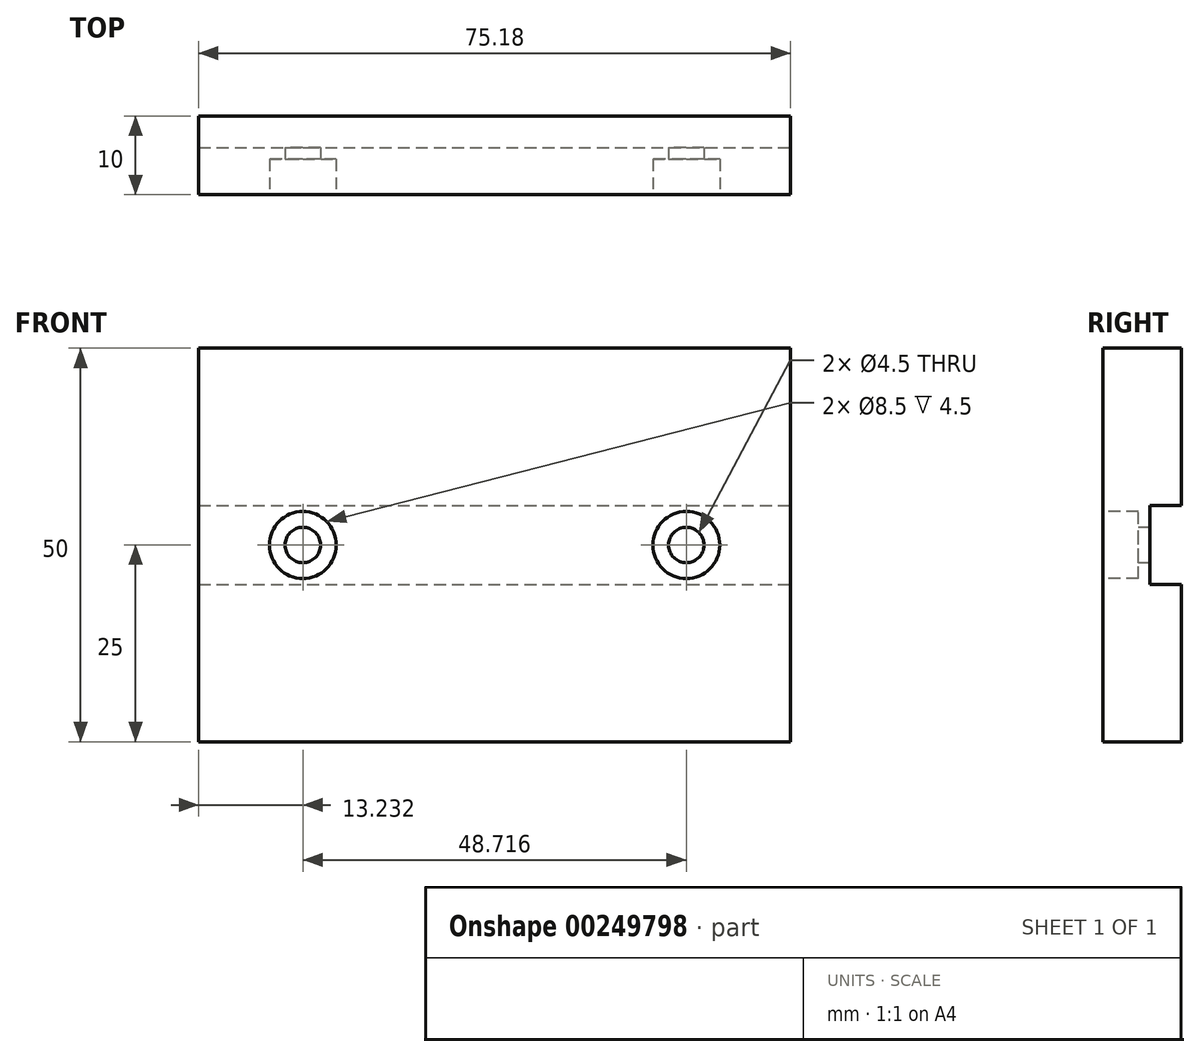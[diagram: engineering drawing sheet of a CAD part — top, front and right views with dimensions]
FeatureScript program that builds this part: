
annotation { "Feature Type Name" : "Feature", "Feature Type Description" : "" }
export const myFeature = defineFeature(function(context is Context, id is Id, definition is map)
    precondition{}
    {
        {
            var Q0;
            Q0=qCreatedBy(makeId("Front.planeOp"),FACE);
            var sketch = newSketch(context, id + "F0", { "sketchPlane" : qUnion([Q0])});
            skLineSegment(sketch, "E0.bottom", {"start": v(-37.6, 25) * mm, "end": v(37.6, 25) * mm});
            skLineSegment(sketch, "E0.top", {"start": v(-37.6, -25) * mm, "end": v(37.6, -25) * mm});
            skLineSegment(sketch, "E0.left", {"start": v(-37.6, 25) * mm, "end": v(-37.6, -25) * mm});
            skLineSegment(sketch, "E0.right", {"start": v(37.6, 25) * mm, "end": v(37.6, -25) * mm});
            skPoint(sketch, "E0.middle", {"position": v(0, 0) * mm});
            skSolve(sketch);
        }
        {
            var Q0;
            Q0=makeQuery(id+"F0.imprint","IMPRINT",FACE,{"disambiguationData":[TD([[makeQuery(id+"F0.imprint","IMPRINT",EDGE,{"derivedFrom":sQuery(id+"F0.wireOp",EDGE,"E0.bottom")}),-1.0]])]});
            extrude(context, id + "F1", {"entities" : qUnion([Q0]), "depth" : 10 * mm});
        }
        {
            var Q0;
            Q0=makeQuery(id+"F1.opExtrude","SWEPT_FACE",FACE,{"disambiguationData":[OSD([sQuery(id+"F0.wireOp",EDGE,"E0.right")])]});
            var sketch = newSketch(context, id + "F2", { "sketchPlane" : qUnion([Q0])});
            skLineSegment(sketch, "E1.bottom", {"start": v(-4, 5) * mm, "end": v(0, 5) * mm});
            skLineSegment(sketch, "E1.top", {"start": v(-4, -5) * mm, "end": v(0, -5) * mm});
            skLineSegment(sketch, "E1.left", {"start": v(-4, 5) * mm, "end": v(-4, -5) * mm});
            skLineSegment(sketch, "E1.right", {"start": v(0, 5) * mm, "end": v(0, -5) * mm});
            skSolve(sketch);
        }
        {
            var Q0;
            Q0=makeQuery(id+"F2.imprint","IMPRINT",FACE,{"disambiguationData":[TD([[makeQuery(id+"F2.imprint","IMPRINT",EDGE,{"derivedFrom":sQuery(id+"F2.wireOp",EDGE,"E1.bottom")}),-1.0]])]});
            extrude(context, id + "F3", {"entities" : qUnion([Q0]), "operationType" : NewBodyOperationType.REMOVE, "endBound" : BoundingType.THROUGH_ALL, "oppositeDirection" : true, "depth" : 25 * mm});
        }
        {
            var Q0;
            Q0=makeQuery(id+"F1.opExtrude","CAP_FACE",FACE,{"disambiguationData":[OSD([sQuery(id+"F0.wireOp",EDGE,"E0.bottom"),sQuery(id+"F0.wireOp",EDGE,"E0.top"),sQuery(id+"F0.wireOp",EDGE,"E0.left"),sQuery(id+"F0.wireOp",EDGE,"E0.right")])],"isStart":false});
            var sketch = newSketch(context, id + "F4", { "sketchPlane" : qUnion([Q0])});
            skLineSegment(sketch, "E2", {"start": v(-37.6, 0) * mm, "end": v(37.6, 0) * mm, "construction": true});
            skLineSegment(sketch, "E3", {"start": v(0, 25) * mm, "end": v(0, -25) * mm, "construction": true});
            skPoint(sketch, "E4", {"position": v(-24.36, 0) * mm});
            skPoint(sketch, "E5.MirrorP", {"position": v(24.36, 0) * mm});
            skSolve(sketch);
        }
        {
            var Q0;
            Q0=sQuery(id+"F4.wireOp",VERTEX,"E4");
            var Q1;
            Q1=sQuery(id+"F4.wireOp",VERTEX,"E5.MirrorP");
            var Q2;
            Q2=makeQuery(id+"F1.opExtrude","SWEPT_BODY",BODY,{"disambiguationData":[OSD([sQuery(id+"F0.wireOp",EDGE,"E0.bottom"),sQuery(id+"F0.wireOp",EDGE,"E0.top"),sQuery(id+"F0.wireOp",EDGE,"E0.left"),sQuery(id+"F0.wireOp",EDGE,"E0.right")])]});
            hole(context, id + "F5", {"style" : HoleStyle.C_BORE, "endStyle" : HoleEndStyle.THROUGH, "holeDiameter" : 4.5 * mm, "cBoreDiameter" : 8.5 * mm, "cBoreDepth" : 4.5 * mm, "tappedDepth" : 12 * mm, "tapClearance" : 3, "locations" : qUnion([Q0, Q1]), "scope" : qUnion([Q2])});
        }
    });
